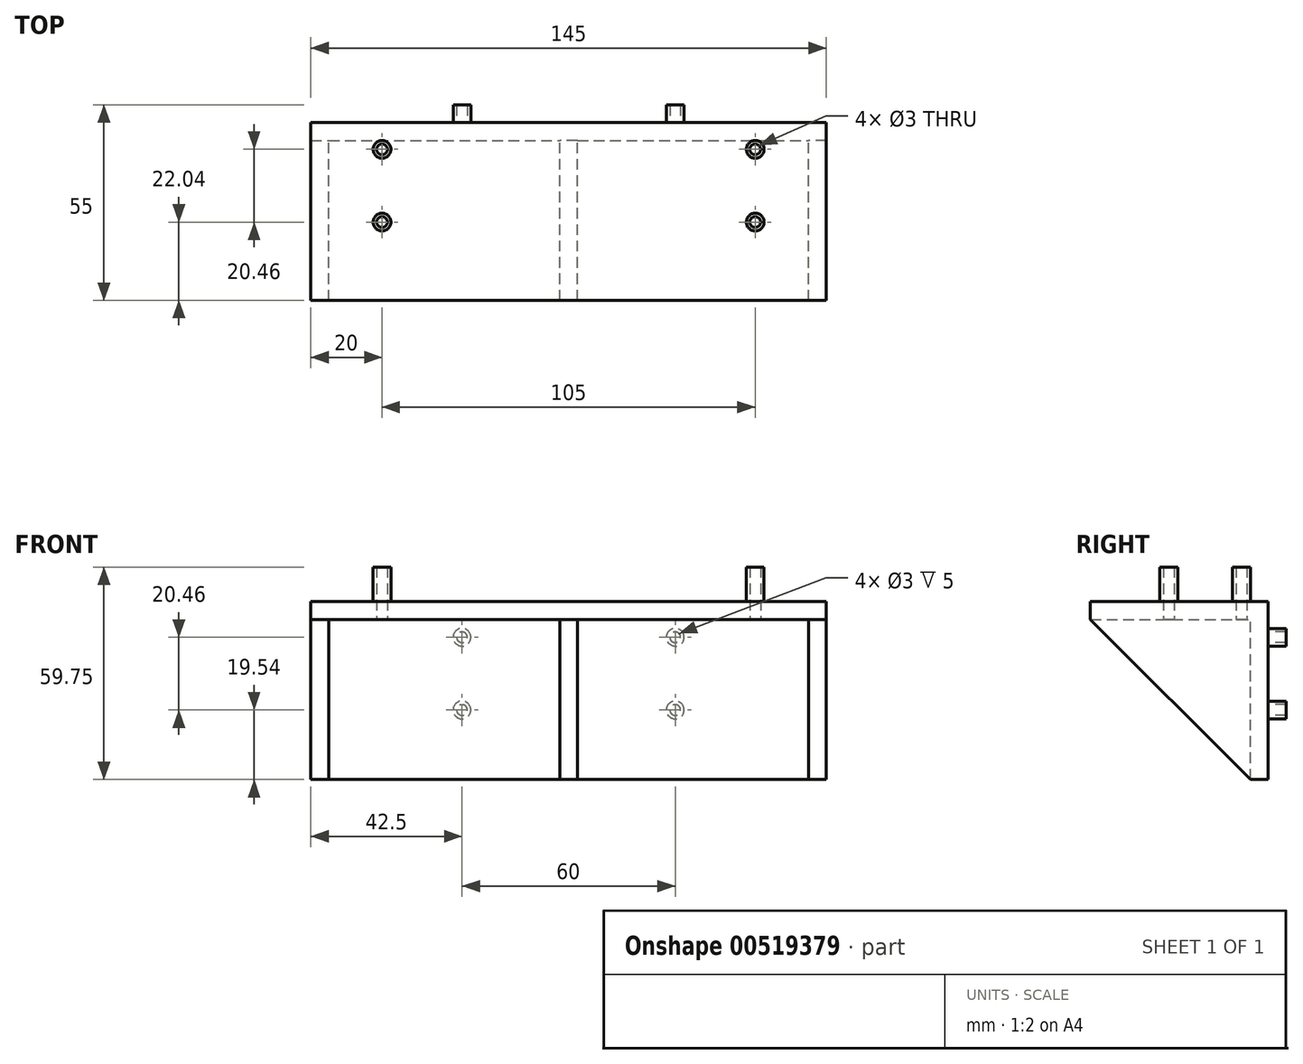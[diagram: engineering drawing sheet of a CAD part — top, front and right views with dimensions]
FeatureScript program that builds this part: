
annotation { "Feature Type Name" : "Feature", "Feature Type Description" : "" }
export const myFeature = defineFeature(function(context is Context, id is Id, definition is map)
    precondition{}
    {
        {
            var Q0;
            Q0=qCreatedBy(makeId("Top.planeOp"),FACE);
            var sketch = newSketch(context, id + "F0", { "sketchPlane" : qUnion([Q0])});
            skLineSegment(sketch, "E0.bottom", {"start": v(0, 0) * mm, "end": v(145, 0) * mm});
            skLineSegment(sketch, "E0.top", {"start": v(0, 50) * mm, "end": v(145, 50) * mm});
            skLineSegment(sketch, "E0.left", {"start": v(0, 0) * mm, "end": v(0, 50) * mm});
            skLineSegment(sketch, "E0.right", {"start": v(145, 0) * mm, "end": v(145, 50) * mm});
            skSolve(sketch);
        }
        {
            var Q0;
            Q0=makeQuery(id+"F0.imprint","IMPRINT",FACE,{"disambiguationData":[TD([[makeQuery(id+"F0.imprint","IMPRINT",EDGE,{"derivedFrom":sQuery(id+"F0.wireOp",EDGE,"E0.bottom")}),1.0]])]});
            extrude(context, id + "F1", {"entities" : qUnion([Q0]), "depth" : 5 * mm, "offsetDistance" : 25 * mm});
        }
        {
            var Q0;
            Q0=makeQuery(id+"F1.opExtrude","CAP_FACE",FACE,{"disambiguationData":[OSD([sQuery(id+"F0.wireOp",EDGE,"E0.bottom"),sQuery(id+"F0.wireOp",EDGE,"E0.top"),sQuery(id+"F0.wireOp",EDGE,"E0.left"),sQuery(id+"F0.wireOp",EDGE,"E0.right")])],"isStart":false});
            var sketch = newSketch(context, id + "F2", { "sketchPlane" : qUnion([Q0])});
            skCircle(sketch, "E1", {"center": v(20, 42.5) * mm, "radius": 2.5 * mm});
            skCircle(sketch, "E2", {"center": v(20, 22.04) * mm, "radius": 2.5 * mm});
            skCircle(sketch, "E3", {"center": v(125, 42.5) * mm, "radius": 2.5 * mm});
            skCircle(sketch, "E4", {"center": v(125, 22.04) * mm, "radius": 2.5 * mm});
            skCircle(sketch, "E5", {"center": v(20, 42.5) * mm, "radius": 1.5 * mm});
            skCircle(sketch, "E6", {"center": v(20, 22.04) * mm, "radius": 1.5 * mm});
            skCircle(sketch, "E7", {"center": v(125, 42.5) * mm, "radius": 1.5 * mm});
            skCircle(sketch, "E8", {"center": v(125, 22.04) * mm, "radius": 1.5 * mm});
            skSolve(sketch);
        }
        {
            var Q0;
            Q0 = qSketchRegion(id + "F2", true);
            extrude(context, id + "F3", {"entities" : qUnion([Q0]), "operationType" : NewBodyOperationType.ADD, "depth" : 9.75 * mm, "offsetDistance" : 25 * mm});
        }
        {
            var Q0;
            {var subQ0=sQuery(id+"F0.wireOp",EDGE,"E0.left");var subQ1=sQuery(id+"F0.wireOp",EDGE,"E0.top");var subQ2=sQuery(id+"F0.wireOp",EDGE,"E0.right");var subQ3=sQuery(id+"F0.wireOp",EDGE,"E0.bottom");Q0=makeQuery(id+"F3.boolean.opBoolean","SPLIT",FACE,{"disambiguationData":[TD([makeQuery(id+"F1.opExtrude","SWEPT_FACE",FACE,{"disambiguationData":[OSD([subQ3])]})])],"derivedFrom":makeQuery(id+"F1.opExtrude","CAP_FACE",FACE,{"disambiguationData":[OSD([subQ3,subQ1,subQ0,subQ2])],"isStart":false})});}
            var sketch = newSketch(context, id + "F4", { "sketchPlane" : qUnion([Q0])});
            skCircle(sketch, "E9", {"center": v(20, 42.5) * mm, "radius": 1.5 * mm});
            skCircle(sketch, "E10", {"center": v(20, 22.04) * mm, "radius": 1.5 * mm});
            skCircle(sketch, "E11", {"center": v(125, 42.5) * mm, "radius": 1.5 * mm});
            skCircle(sketch, "E12", {"center": v(125, 22.04) * mm, "radius": 1.5 * mm});
            skSolve(sketch);
        }
        {
            var Q0;
            Q0 = qSketchRegion(id + "F4", true);
            extrude(context, id + "F5", {"entities" : qUnion([Q0]), "operationType" : NewBodyOperationType.REMOVE, "oppositeDirection" : true, "depth" : 25 * mm, "offsetDistance" : 25 * mm});
        }
        {
            var Q0;
            Q0=makeQuery(id+"F1.opExtrude","SWEPT_FACE",FACE,{"disambiguationData":[OSD([sQuery(id+"F0.wireOp",EDGE,"E0.right")])]});
            var sketch = newSketch(context, id + "F6", { "sketchPlane" : qUnion([Q0])});
            skLineSegment(sketch, "E13", {"start": v(50, 0) * mm, "end": v(50, -45) * mm});
            skLineSegment(sketch, "E14", {"start": v(50, -45) * mm, "end": v(45, -45) * mm});
            skLineSegment(sketch, "E15", {"start": v(45, -45) * mm, "end": v(45, 0) * mm});
            skLineSegment(sketch, "E16", {"start": v(45, 0) * mm, "end": v(50, 0) * mm});
            skSolve(sketch);
        }
        {
            var Q0;
            Q0=makeQuery(id+"F6.imprint","IMPRINT",FACE,{"disambiguationData":[TD([[makeQuery(id+"F6.imprint","IMPRINT",EDGE,{"derivedFrom":sQuery(id+"F6.wireOp",EDGE,"E13")}),-1.0]])]});
            var Q1;
            Q1=makeQuery(id+"F1.opExtrude","SWEPT_FACE",FACE,{"disambiguationData":[OSD([sQuery(id+"F0.wireOp",EDGE,"E0.left")])]});
            extrude(context, id + "F7", {"entities" : qUnion([Q0]), "operationType" : NewBodyOperationType.ADD, "endBound" : BoundingType.UP_TO_SURFACE, "oppositeDirection" : true, "depth" : 25 * mm, "endBoundEntityFace" : qUnion([Q1]), "offsetDistance" : 25 * mm});
        }
        {
            var Q0;
            {var subQ0=sQuery(id+"F0.wireOp",EDGE,"E0.left");Q0=makeQuery(id+"F7.boolean.opBoolean","MERGE",FACE,{"derivedFrom":[makeQuery(id+"F1.opExtrude","SWEPT_FACE",FACE,{"disambiguationData":[OSD([subQ0])]}),makeQuery(id+"F7.opExtrude","CAP_FACE",FACE,{"disambiguationData":[OSD([subQ0])],"isStart":false})]});}
            var sketch = newSketch(context, id + "F8", { "sketchPlane" : qUnion([Q0])});
            skLineSegment(sketch, "E17", {"start": v(-45, -45) * mm, "end": v(-45, 0) * mm});
            skLineSegment(sketch, "E18", {"start": v(-45, 0) * mm, "end": v(0, 0) * mm});
            skLineSegment(sketch, "E19", {"start": v(0, 0) * mm, "end": v(-45, -45) * mm});
            skSolve(sketch);
        }
        {
            var Q0;
            Q0=makeQuery(id+"F8.imprint","IMPRINT",FACE,{"disambiguationData":[TD([[makeQuery(id+"F8.imprint","IMPRINT",EDGE,{"derivedFrom":sQuery(id+"F8.wireOp",EDGE,"E17")}),-1.0]])]});
            extrude(context, id + "F9", {"entities" : qUnion([Q0]), "operationType" : NewBodyOperationType.ADD, "oppositeDirection" : true, "depth" : 5 * mm, "offsetDistance" : 25 * mm});
        }
        {
            var Q0;
            Q0 = qSketchRegion(id + "F8", true);
            extrude(context, id + "F10", {"entities" : qUnion([Q0]), "operationType" : NewBodyOperationType.ADD, "oppositeDirection" : true, "depth" : 75 * mm, "offsetDistance" : 25 * mm, "hasSecondDirection" : true, "secondDirectionOppositeDirection" : true, "secondDirectionDepth" : 70 * mm});
        }
        {
            var Q0;
            Q0 = qSketchRegion(id + "F8", true);
            extrude(context, id + "F11", {"entities" : qUnion([Q0]), "operationType" : NewBodyOperationType.ADD, "oppositeDirection" : true, "depth" : 145 * mm, "offsetDistance" : 25 * mm, "hasSecondDirection" : true, "secondDirectionOppositeDirection" : true, "secondDirectionDepth" : 140 * mm});
        }
        {
            var Q0;
            Q0=makeQuery(id+"F7.boolean.opBoolean","MERGE",FACE,{"derivedFrom":[makeQuery(id+"F1.opExtrude","SWEPT_FACE",FACE,{"disambiguationData":[OSD([sQuery(id+"F0.wireOp",EDGE,"E0.top")])]}),makeQuery(id+"F7.opExtrude","SWEPT_FACE",FACE,{"disambiguationData":[OSD([sQuery(id+"F6.wireOp",EDGE,"E13")])]})]});
            var sketch = newSketch(context, id + "F12", { "sketchPlane" : qUnion([Q0])});
            skCircle(sketch, "E20", {"center": v(-102.5, -5) * mm, "radius": 2.5 * mm});
            skCircle(sketch, "E21", {"center": v(-102.5, -5) * mm, "radius": 1.5 * mm});
            skCircle(sketch, "E22", {"center": v(-102.5, -25.46) * mm, "radius": 2.5 * mm});
            skCircle(sketch, "E23", {"center": v(-102.5, -25.46) * mm, "radius": 1.5 * mm});
            skCircle(sketch, "E24", {"center": v(-42.5, -5) * mm, "radius": 2.5 * mm});
            skCircle(sketch, "E25", {"center": v(-42.5, -5) * mm, "radius": 1.5 * mm});
            skCircle(sketch, "E26", {"center": v(-42.5, -25.46) * mm, "radius": 1.5 * mm});
            skCircle(sketch, "E27", {"center": v(-42.5, -25.46) * mm, "radius": 2.5 * mm});
            skSolve(sketch);
        }
        {
            var Q0;
            Q0 = qSketchRegion(id + "F12", true);
            extrude(context, id + "F13", {"entities" : qUnion([Q0]), "operationType" : NewBodyOperationType.ADD, "depth" : 5 * mm, "offsetDistance" : 25 * mm});
        }
    });
